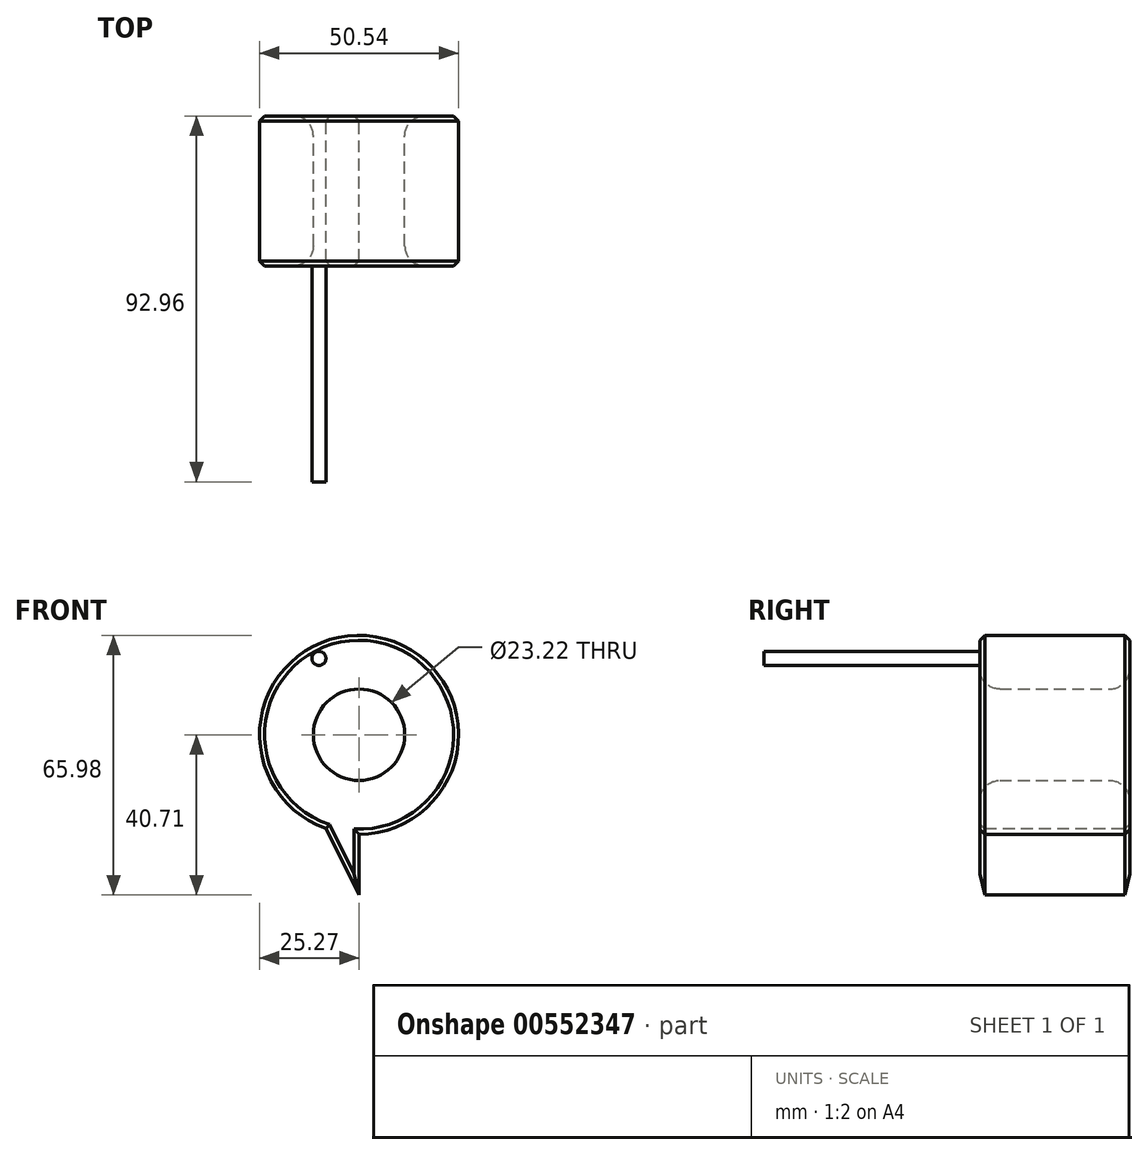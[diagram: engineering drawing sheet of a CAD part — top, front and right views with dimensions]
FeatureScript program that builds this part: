
annotation { "Feature Type Name" : "Feature", "Feature Type Description" : "" }
export const myFeature = defineFeature(function(context is Context, id is Id, definition is map)
    precondition{}
    {
        {
            var Q0;
            Q0=qCreatedBy(makeId("Front.planeOp"),FACE);
            var sketch = newSketch(context, id + "F0", { "sketchPlane" : qUnion([Q0])});
            skLineSegment(sketch, "E0", {"start": v(0, -25.27) * mm, "end": v(0, -40.7) * mm});
            skLineSegment(sketch, "E1", {"start": v(-8.4, -23.83) * mm, "end": v(0, -40.7) * mm});
            skArc(sketch, "E2", {"start": v(0, -25.27) * mm, "mid": v(4.26, 24.91) * mm, "end": v(-8.4, -23.83) * mm});
            skCircle(sketch, "E3", {"center": v(0, 0) * mm, "radius": 11.61 * mm});
            skSolve(sketch);
        }
        {
            var Q0;
            Q0 = qSketchRegion(id + "F0", true);
            extrude(context, id + "F1", {"entities" : qUnion([Q0]), "depth" : 38.1 * mm, "offsetDistance" : 25.4 * mm});
        }
        {
            var Q0;
            Q0=makeQuery(id+"F1.opExtrude","CAP_EDGE",EDGE,{"disambiguationData":[OSD([sQuery(id+"F0.wireOp",EDGE,"E3")])],"isStart":true});
            var Q1;
            Q1=makeQuery(id+"F1.opExtrude","CAP_EDGE",EDGE,{"disambiguationData":[OSD([sQuery(id+"F0.wireOp",EDGE,"E3")])],"isStart":false});
            fillet(context, id + "F2", {"entities" : qUnion([Q0, Q1]), "radius" : 5.08 * mm, "tangentPropagation" : true, "allowEdgeOverflow" : false});
        }
        {
            var Q0;
            Q0=makeQuery(id+"F1.opExtrude","CAP_EDGE",EDGE,{"disambiguationData":[OSD([sQuery(id+"F0.wireOp",EDGE,"E2")])],"isStart":false});
            var Q1;
            Q1=makeQuery(id+"F1.opExtrude","CAP_EDGE",EDGE,{"disambiguationData":[OSD([sQuery(id+"F0.wireOp",EDGE,"E0")])],"isStart":false});
            var Q2;
            Q2=makeQuery(id+"F1.opExtrude","CAP_EDGE",EDGE,{"disambiguationData":[OSD([sQuery(id+"F0.wireOp",EDGE,"E2")])],"isStart":true});
            var Q3;
            Q3=makeQuery(id+"F1.opExtrude","CAP_EDGE",EDGE,{"disambiguationData":[OSD([sQuery(id+"F0.wireOp",EDGE,"E0")])],"isStart":true});
            var Q4;
            Q4=makeQuery(id+"F1.opExtrude","CAP_EDGE",EDGE,{"disambiguationData":[OSD([sQuery(id+"F0.wireOp",EDGE,"E1")])],"isStart":true});
            var Q5;
            Q5=makeQuery(id+"F1.opExtrude","CAP_EDGE",EDGE,{"disambiguationData":[OSD([sQuery(id+"F0.wireOp",EDGE,"E1")])],"isStart":false});
            chamfer(context, id + "F3", {"entities" : qUnion([Q0, Q1, Q2, Q3, Q4, Q5]), "width" : 1.27 * mm, "tangentPropagation" : true});
        }
        {
            var Q0;
            Q0=makeQuery(id+"F1.opExtrude","CAP_FACE",FACE,{"disambiguationData":[OSD([sQuery(id+"F0.wireOp",EDGE,"E0"),sQuery(id+"F0.wireOp",EDGE,"E1"),sQuery(id+"F0.wireOp",EDGE,"E2"),sQuery(id+"F0.wireOp",EDGE,"E3")])],"isStart":false});
            var sketch = newSketch(context, id + "F4", { "sketchPlane" : qUnion([Q0])});
            skLineSegment(sketch, "E4", {"start": v(-12.63, 17.45) * mm, "end": v(-5.96, 15.59) * mm});
            skLineSegment(sketch, "E5", {"start": v(-5.96, 15.59) * mm, "end": v(-3.3, 23.77) * mm});
            skLineSegment(sketch, "E6", {"start": v(-3.3, 23.77) * mm, "end": v(7.16, 15.59) * mm});
            skLineSegment(sketch, "E7", {"start": v(7.16, 15.59) * mm, "end": v(18.25, 15.59) * mm});
            skLineSegment(sketch, "E8", {"start": v(18.25, 15.59) * mm, "end": v(17.23, 4.83) * mm});
            skLineSegment(sketch, "E9", {"start": v(15.22, -6.85) * mm, "end": v(15.22, -18.56) * mm});
            skLineSegment(sketch, "E10", {"start": v(15.22, -18.56) * mm, "end": v(6.61, -15.33) * mm});
            skLineSegment(sketch, "E11", {"start": v(6.61, -15.33) * mm, "end": v(6.61, -22.8) * mm});
            skLineSegment(sketch, "E12", {"start": v(-11.31, -12.27) * mm, "end": v(-20.63, -12.27) * mm});
            skLineSegment(sketch, "E13", {"start": v(-20.63, -12.27) * mm, "end": v(-17.3, 0) * mm});
            skLineSegment(sketch, "E14", {"start": v(-17.3, 0) * mm, "end": v(-23.94, 1.8) * mm});
            skLineSegment(sketch, "E15", {"start": v(-11.31, -12.27) * mm, "end": v(-11.31, -21.17) * mm});
            skLineSegment(sketch, "E16", {"start": v(-23.94, 1.8) * mm, "end": v(-15.6, 5.95) * mm});
            skLineSegment(sketch, "E17", {"start": v(-15.6, 5.95) * mm, "end": v(-19.45, 14.07) * mm});
            skLineSegment(sketch, "E18", {"start": v(-19.45, 14.07) * mm, "end": v(-12.63, 17.45) * mm});
            skLineSegment(sketch, "E19", {"start": v(17.23, 4.83) * mm, "end": v(22.25, 0) * mm});
            skLineSegment(sketch, "E20", {"start": v(22.25, 0) * mm, "end": v(15.22, -6.85) * mm});
            skLineSegment(sketch, "E21", {"start": v(-11.31, -21.17) * mm, "end": v(-5.06, -16.72) * mm});
            skPoint(sketch, "E21.endSnap0", {"position": v(-11.31, -16.72) * mm});
            skLineSegment(sketch, "E22", {"start": v(-5.06, -16.72) * mm, "end": v(6.61, -22.8) * mm});
            skSolve(sketch);
        }
        {
            var Q0;
            {var subQ0=sQuery(id+"F4.wireOp",EDGE,"E6");Q0=makeQuery(id+"F4.imprint","IMPRINT",FACE,{"disambiguationData":[TD([[makeQuery(id+"F4.imprint","IMPRINT",EDGE,{"derivedFrom":subQ0}),1.0]])]});}
            var sketch = newSketch(context, id + "F5", { "sketchPlane" : qUnion([Q0])});
            skCircle(sketch, "E23", {"center": v(-10.2, 19.4) * mm, "radius": 1.78 * mm});
            skSolve(sketch);
        }
        {
            var Q0;
            Q0 = qSketchRegion(id + "F5", true);
            extrude(context, id + "F6", {"entities" : qUnion([Q0]), "operationType" : NewBodyOperationType.ADD, "depth" : 54.86 * mm, "offsetDistance" : 25.4 * mm});
        }
    });
